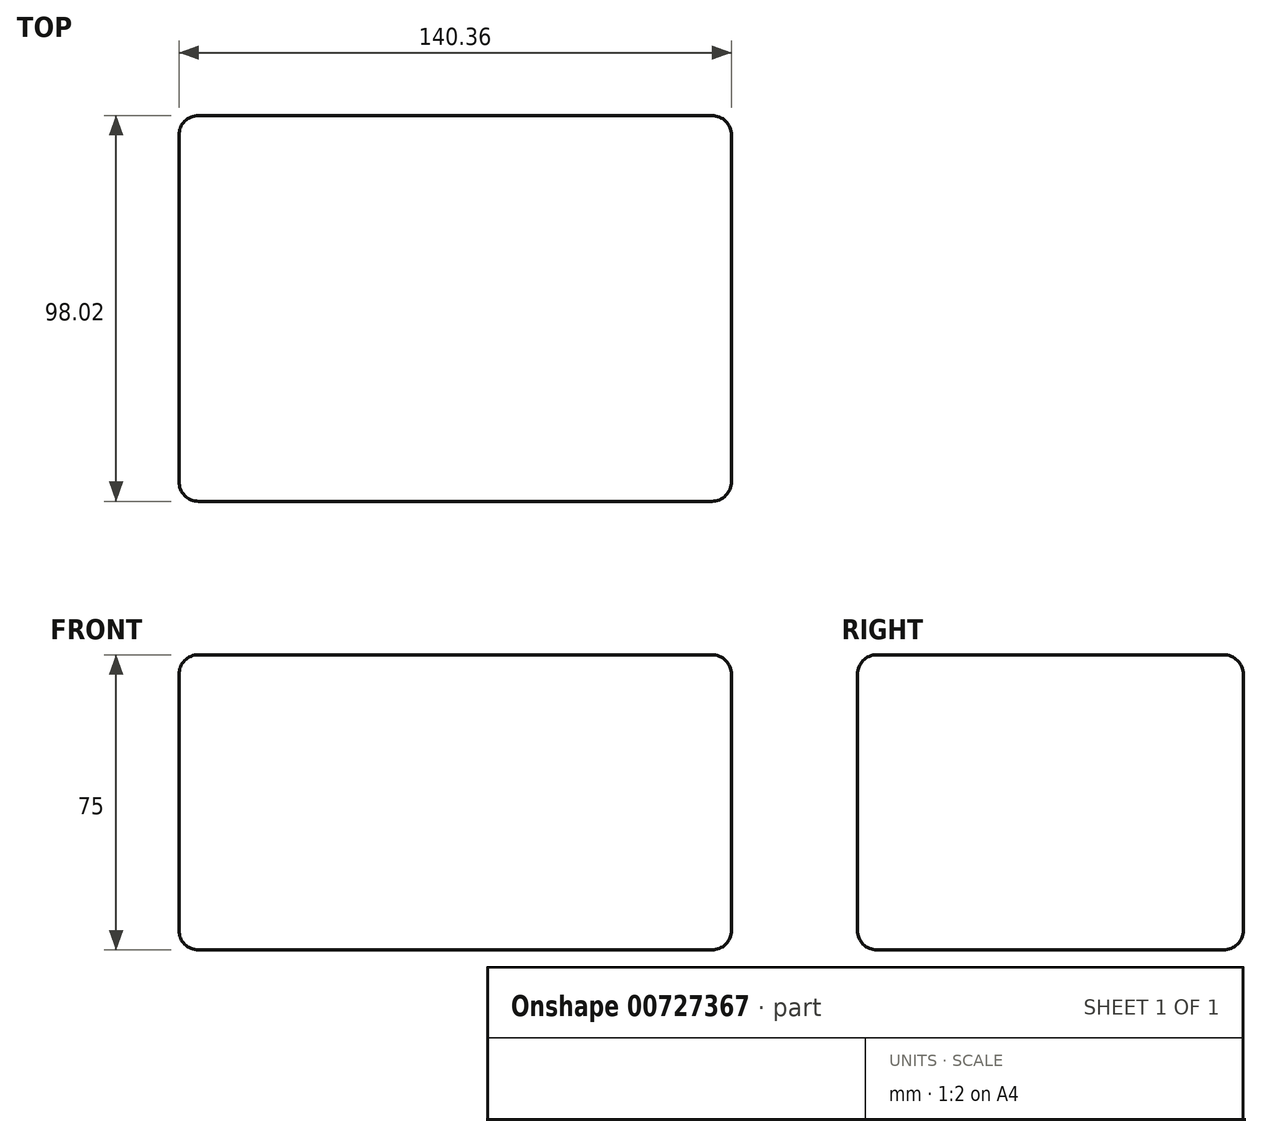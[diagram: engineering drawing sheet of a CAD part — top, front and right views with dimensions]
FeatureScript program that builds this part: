
annotation { "Feature Type Name" : "Feature", "Feature Type Description" : "" }
export const myFeature = defineFeature(function(context is Context, id is Id, definition is map)
    precondition{}
    {
        {
            var Q0;
            Q0=qCreatedBy(makeId("Top.planeOp"),FACE);
            var sketch = newSketch(context, id + "F0", { "sketchPlane" : qUnion([Q0])});
            skLineSegment(sketch, "E0.bottom", {"start": v(-121.63, 35.92) * mm, "end": v(18.73, 35.92) * mm});
            skLineSegment(sketch, "E0.top", {"start": v(-121.63, -62.1) * mm, "end": v(18.73, -62.1) * mm});
            skLineSegment(sketch, "E0.left", {"start": v(-121.63, 35.92) * mm, "end": v(-121.63, -62.1) * mm});
            skLineSegment(sketch, "E0.right", {"start": v(18.73, 35.92) * mm, "end": v(18.73, -62.1) * mm});
            skSolve(sketch);
        }
        {
            var Q0;
            Q0=makeQuery(id+"F0.imprint","IMPRINT",FACE,{"disambiguationData":[TD([[makeQuery(id+"F0.imprint","IMPRINT",EDGE,{"derivedFrom":sQuery(id+"F0.wireOp",EDGE,"E0.bottom")}),-1.0]])]});
            extrude(context, id + "F1", {"entities" : qUnion([Q0]), "depth" : 25 * mm, "offsetDistance" : 25.4 * mm});
        }
        {
            var Q0;
            Q0=makeQuery(id+"F1.opExtrude","CAP_FACE",FACE,{"disambiguationData":[OSD([sQuery(id+"F0.wireOp",EDGE,"E0.bottom"),sQuery(id+"F0.wireOp",EDGE,"E0.top"),sQuery(id+"F0.wireOp",EDGE,"E0.left"),sQuery(id+"F0.wireOp",EDGE,"E0.right")])],"isStart":true});
            extrude(context, id + "F2", {"entities" : qUnion([Q0]), "operationType" : NewBodyOperationType.ADD, "depth" : 50 * mm, "offsetDistance" : 25 * mm});
        }
        {
            var Q0;
            Q0=makeQuery(id+"F2.opExtrude","CAP_FACE",FACE,{"disambiguationData":[OSD([sQuery(id+"F0.wireOp",EDGE,"E0.bottom"),sQuery(id+"F0.wireOp",EDGE,"E0.top"),sQuery(id+"F0.wireOp",EDGE,"E0.left"),sQuery(id+"F0.wireOp",EDGE,"E0.right")])],"isStart":false});
            extrude(context, id + "F3", {"entities" : qUnion([Q0]), "operationType" : NewBodyOperationType.ADD, "oppositeDirection" : true, "depth" : 25 * mm, "offsetDistance" : 25 * mm});
        }
        {
            var Q0;
            Q0=makeQuery(id+"F1.opExtrude","CAP_EDGE",EDGE,{"disambiguationData":[OSD([sQuery(id+"F0.wireOp",EDGE,"E0.right")])],"isStart":false});
            var Q1;
            Q1=makeQuery(id+"F1.opExtrude","CAP_EDGE",EDGE,{"disambiguationData":[OSD([sQuery(id+"F0.wireOp",EDGE,"E0.left")])],"isStart":false});
            var Q2;
            Q2=makeQuery(id+"F1.opExtrude","CAP_EDGE",EDGE,{"disambiguationData":[OSD([sQuery(id+"F0.wireOp",EDGE,"E0.bottom")])],"isStart":false});
            var Q3;
            Q3=makeQuery(id+"F1.opExtrude","CAP_EDGE",EDGE,{"disambiguationData":[OSD([sQuery(id+"F0.wireOp",EDGE,"E0.top")])],"isStart":false});
            var Q4;
            Q4=makeQuery(id+"F2.opExtrude","CAP_EDGE",EDGE,{"disambiguationData":[OSD([sQuery(id+"F0.wireOp",EDGE,"E0.bottom")])],"isStart":false});
            var Q5;
            Q5=makeQuery(id+"F2.opExtrude","CAP_EDGE",EDGE,{"disambiguationData":[OSD([sQuery(id+"F0.wireOp",EDGE,"E0.left")])],"isStart":false});
            var Q6;
            Q6=makeQuery(id+"F2.opExtrude","CAP_EDGE",EDGE,{"disambiguationData":[OSD([sQuery(id+"F0.wireOp",EDGE,"E0.top")])],"isStart":false});
            var Q7;
            Q7=makeQuery(id+"F2.opExtrude","CAP_EDGE",EDGE,{"disambiguationData":[OSD([sQuery(id+"F0.wireOp",EDGE,"E0.right")])],"isStart":false});
            fillet(context, id + "F4", {"entities" : qUnion([Q0, Q1, Q2, Q3, Q4, Q5, Q6, Q7]), "radius" : 5 * mm, "tangentPropagation" : true, "allowEdgeOverflow" : false});
        }
        {
            var Q0;
            {var subQ0=sQuery(id+"F0.wireOp",EDGE,"E0.left");var subQ1=sQuery(id+"F0.wireOp",EDGE,"E0.bottom");Q0=makeQuery(id+"F2.boolean.opBoolean","MERGE",EDGE,{"derivedFrom":[makeQuery(id+"F1.opExtrude","SWEPT_EDGE",EDGE,{"disambiguationData":[OSD([subQ1,subQ0])]}),makeQuery(id+"F2.opExtrude","SWEPT_EDGE",EDGE,{"disambiguationData":[OSD([subQ1,subQ0])]})]});}
            var Q1;
            {var subQ0=sQuery(id+"F0.wireOp",EDGE,"E0.right");var subQ1=sQuery(id+"F0.wireOp",EDGE,"E0.bottom");Q1=makeQuery(id+"F2.boolean.opBoolean","MERGE",EDGE,{"derivedFrom":[makeQuery(id+"F1.opExtrude","SWEPT_EDGE",EDGE,{"disambiguationData":[OSD([subQ1,subQ0])]}),makeQuery(id+"F2.opExtrude","SWEPT_EDGE",EDGE,{"disambiguationData":[OSD([subQ1,subQ0])]})]});}
            var Q2;
            {var subQ0=sQuery(id+"F0.wireOp",EDGE,"E0.right");var subQ1=sQuery(id+"F0.wireOp",EDGE,"E0.top");Q2=makeQuery(id+"F2.boolean.opBoolean","MERGE",EDGE,{"derivedFrom":[makeQuery(id+"F1.opExtrude","SWEPT_EDGE",EDGE,{"disambiguationData":[OSD([subQ1,subQ0])]}),makeQuery(id+"F2.opExtrude","SWEPT_EDGE",EDGE,{"disambiguationData":[OSD([subQ1,subQ0])]})]});}
            var Q3;
            {var subQ0=sQuery(id+"F0.wireOp",EDGE,"E0.left");var subQ1=sQuery(id+"F0.wireOp",EDGE,"E0.top");Q3=makeQuery(id+"F2.boolean.opBoolean","MERGE",EDGE,{"derivedFrom":[makeQuery(id+"F1.opExtrude","SWEPT_EDGE",EDGE,{"disambiguationData":[OSD([subQ1,subQ0])]}),makeQuery(id+"F2.opExtrude","SWEPT_EDGE",EDGE,{"disambiguationData":[OSD([subQ1,subQ0])]})]});}
            fillet(context, id + "F5", {"entities" : qUnion([Q0, Q1, Q2, Q3]), "radius" : 5 * mm, "tangentPropagation" : true, "allowEdgeOverflow" : false});
        }
    });
